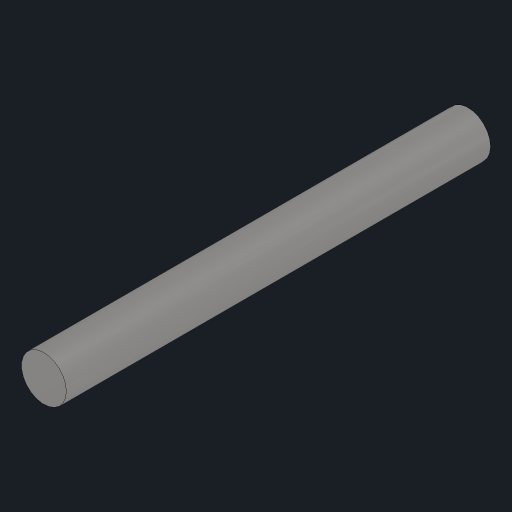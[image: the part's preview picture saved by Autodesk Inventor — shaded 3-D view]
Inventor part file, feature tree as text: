
AUTODESK INVENTOR PART (.ipt)
format: ipt  version: 2023.2 (Build 272271030, 271C)  size: 89,600 bytes
history: native  units: mm
features: extrude x1, sketch x1
ambient origin geometry x8: Origin, YZ Plane, XZ Plane, XY Plane, X Axis, Y Axis, Z Axis, Center Point
bodies: Solid1 (feature_tree)
feature tree (2):
  extrude  "Extrusion1"  Depth=30.0mm TaperAngle=0.0deg
  sketch  "Sketch1"  dims[d0=3.175mm d1=30.0mm d2=0.0mm]
